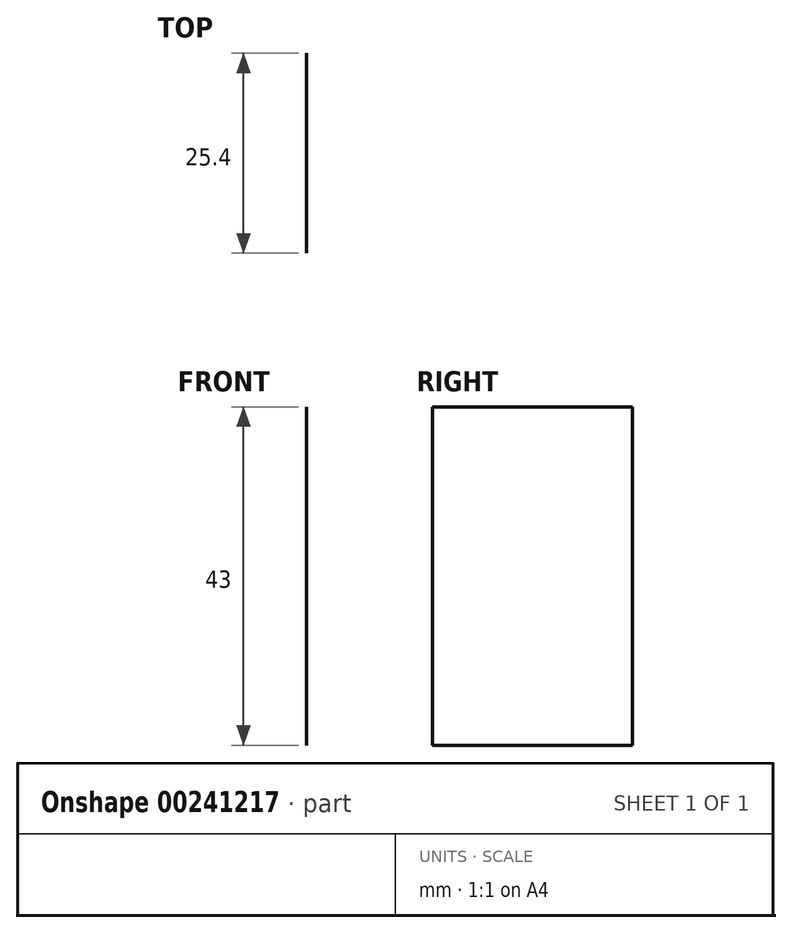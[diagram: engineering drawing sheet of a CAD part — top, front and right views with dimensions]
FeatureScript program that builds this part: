
annotation { "Feature Type Name" : "Feature", "Feature Type Description" : "" }
export const myFeature = defineFeature(function(context is Context, id is Id, definition is map)
    precondition{}
    {
        {
            var Q0;
            Q0=qCreatedBy(makeId("Front.planeOp"),FACE);
            var sketch = newSketch(context, id + "F0", { "sketchPlane" : qUnion([Q0])});
            skLineSegment(sketch, "E0.bottom", {"start": v(-22.18, 21.5) * mm, "end": v(22.18, 21.5) * mm});
            skLineSegment(sketch, "E0.top", {"start": v(-22.18, -21.5) * mm, "end": v(22.18, -21.5) * mm});
            skLineSegment(sketch, "E0.left", {"start": v(-22.18, 21.5) * mm, "end": v(-22.18, -21.5) * mm});
            skLineSegment(sketch, "E0.right", {"start": v(22.18, 21.5) * mm, "end": v(22.18, -21.5) * mm});
            skPoint(sketch, "E0.middle", {"position": v(0, 0) * mm});
            skSolve(sketch);
        }
        {
            var Q0;
            Q0=sQuery(id+"F0.wireOp",EDGE,"E0.left");
            extrude(context, id + "F1", {"bodyType" : ToolBodyType.SURFACE, "surfaceEntities" : qUnion([Q0]), "depth" : 25.4 * mm});
        }
    });
